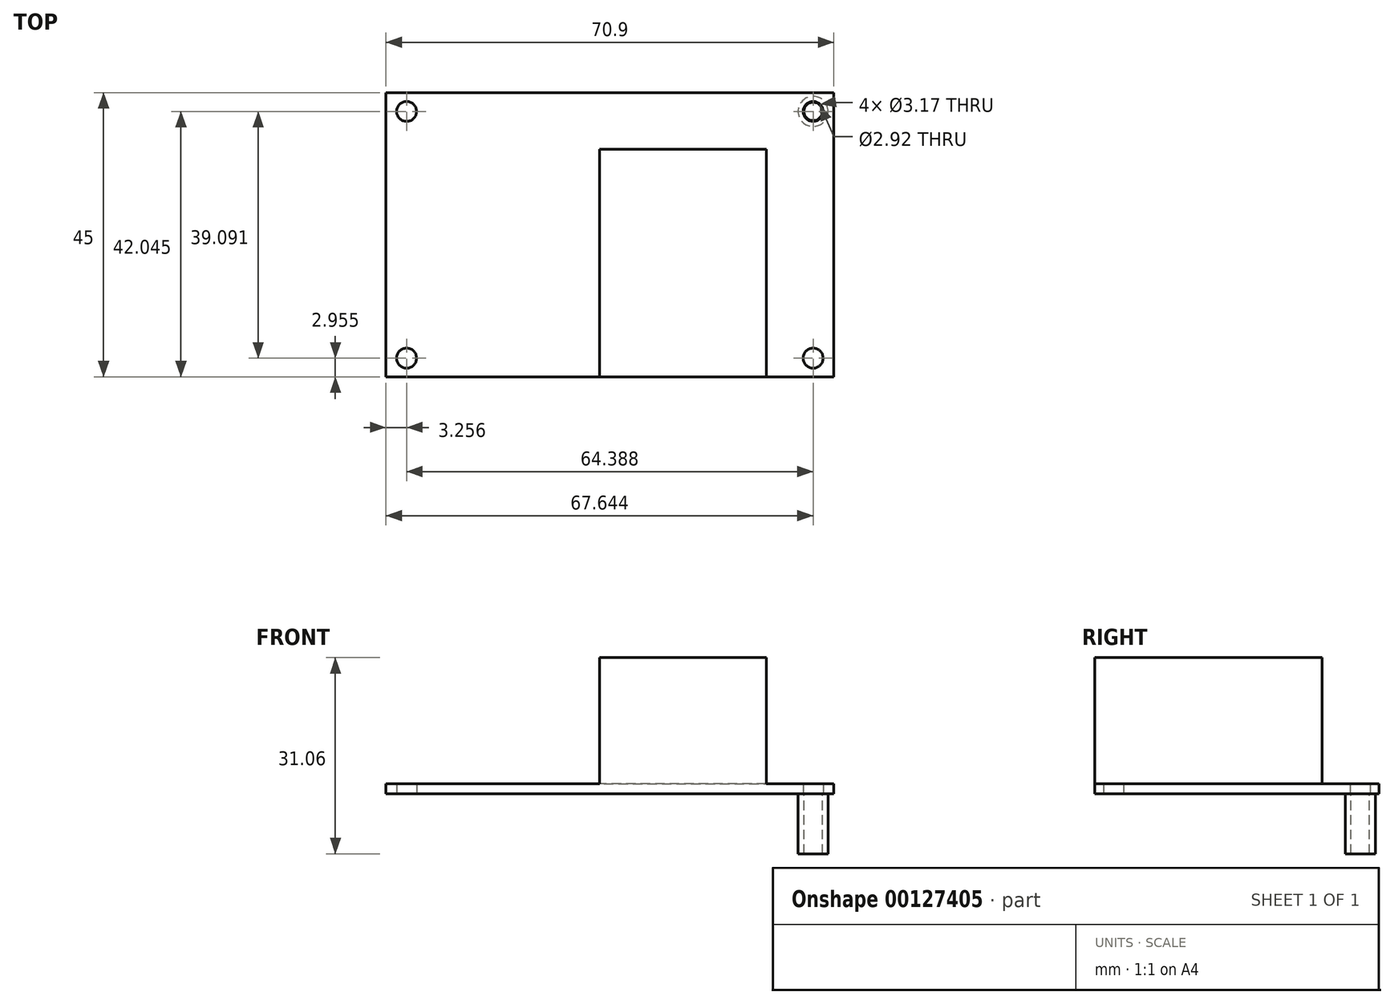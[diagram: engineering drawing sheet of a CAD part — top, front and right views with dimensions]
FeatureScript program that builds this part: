
annotation { "Feature Type Name" : "Feature", "Feature Type Description" : "" }
export const myFeature = defineFeature(function(context is Context, id is Id, definition is map)
    precondition{}
    {
        {
            var Q0;
            Q0=qCreatedBy(makeId("Top.planeOp"),FACE);
            var sketch = newSketch(context, id + "F0", { "sketchPlane" : qUnion([Q0])});
            skLineSegment(sketch, "E0.bottom", {"start": v(-35.45, -22.5) * mm, "end": v(35.45, -22.5) * mm});
            skLineSegment(sketch, "E0.top", {"start": v(-35.44, 22.5) * mm, "end": v(35.44, 22.5) * mm});
            skLineSegment(sketch, "E0.left", {"start": v(-35.45, -22.5) * mm, "end": v(-35.45, 22.5) * mm});
            skLineSegment(sketch, "E0.right", {"start": v(35.45, -22.5) * mm, "end": v(35.45, 22.5) * mm});
            skPoint(sketch, "E0.middle", {"position": v(0, 0) * mm});
            skCircle(sketch, "E1", {"center": v(-32.2, -19.55) * mm, "radius": 1.59 * mm});
            skCircle(sketch, "E2.MirrorC", {"center": v(32.2, -19.55) * mm, "radius": 1.59 * mm});
            skCircle(sketch, "E3.MirrorC", {"center": v(-32.2, 19.55) * mm, "radius": 1.59 * mm});
            skCircle(sketch, "E4.MirrorC", {"center": v(32.2, 19.55) * mm, "radius": 1.59 * mm});
            skSolve(sketch);
        }
        {
            var Q0;
            Q0=qSketchRegion(id+"F0",true);
            extrude(context, id + "F1", {"entities" : qUnion([Q0]), "depth" : 1.57 * mm});
        }
        {
            var Q0;
            Q0=qCreatedBy(makeId("Top.planeOp"),FACE);
            var sketch = newSketch(context, id + "F2", { "sketchPlane" : qUnion([Q0])});
            skLineSegment(sketch, "E5.bottom", {"start": v(-1.64, 13.52) * mm, "end": v(24.78, 13.52) * mm});
            skLineSegment(sketch, "E5.top", {"start": v(-1.64, -22.5) * mm, "end": v(24.78, -22.5) * mm});
            skLineSegment(sketch, "E5.left", {"start": v(-1.64, 13.52) * mm, "end": v(-1.64, -22.5) * mm});
            skLineSegment(sketch, "E5.right", {"start": v(24.78, 13.52) * mm, "end": v(24.78, -22.5) * mm});
            skPoint(sketch, "E5.middle", {"position": v(11.57, -4.5) * mm});
            skSolve(sketch);
        }
        {
            var Q0;
            Q0=qSketchRegion(id+"F2",true);
            extrude(context, id + "F3", {"entities" : qUnion([Q0]), "operationType" : NewBodyOperationType.ADD, "depth" : 21.53 * mm});
        }
        {
            var Q0;
            Q0=qCreatedBy(makeId("Top.planeOp"),FACE);
            var sketch = newSketch(context, id + "F4", { "sketchPlane" : qUnion([Q0])});
            skCircle(sketch, "E6", {"center": v(32.2, 19.55) * mm, "radius": 2.39 * mm});
            skCircle(sketch, "E7", {"center": v(32.2, 19.55) * mm, "radius": 1.46 * mm});
            skSolve(sketch);
        }
        {
            var Q0;
            Q0=qSketchRegion(id+"F4",true);
            extrude(context, id + "F5", {"entities" : qUnion([Q0]), "oppositeDirection" : true, "depth" : 9.52 * mm});
        }
    });
